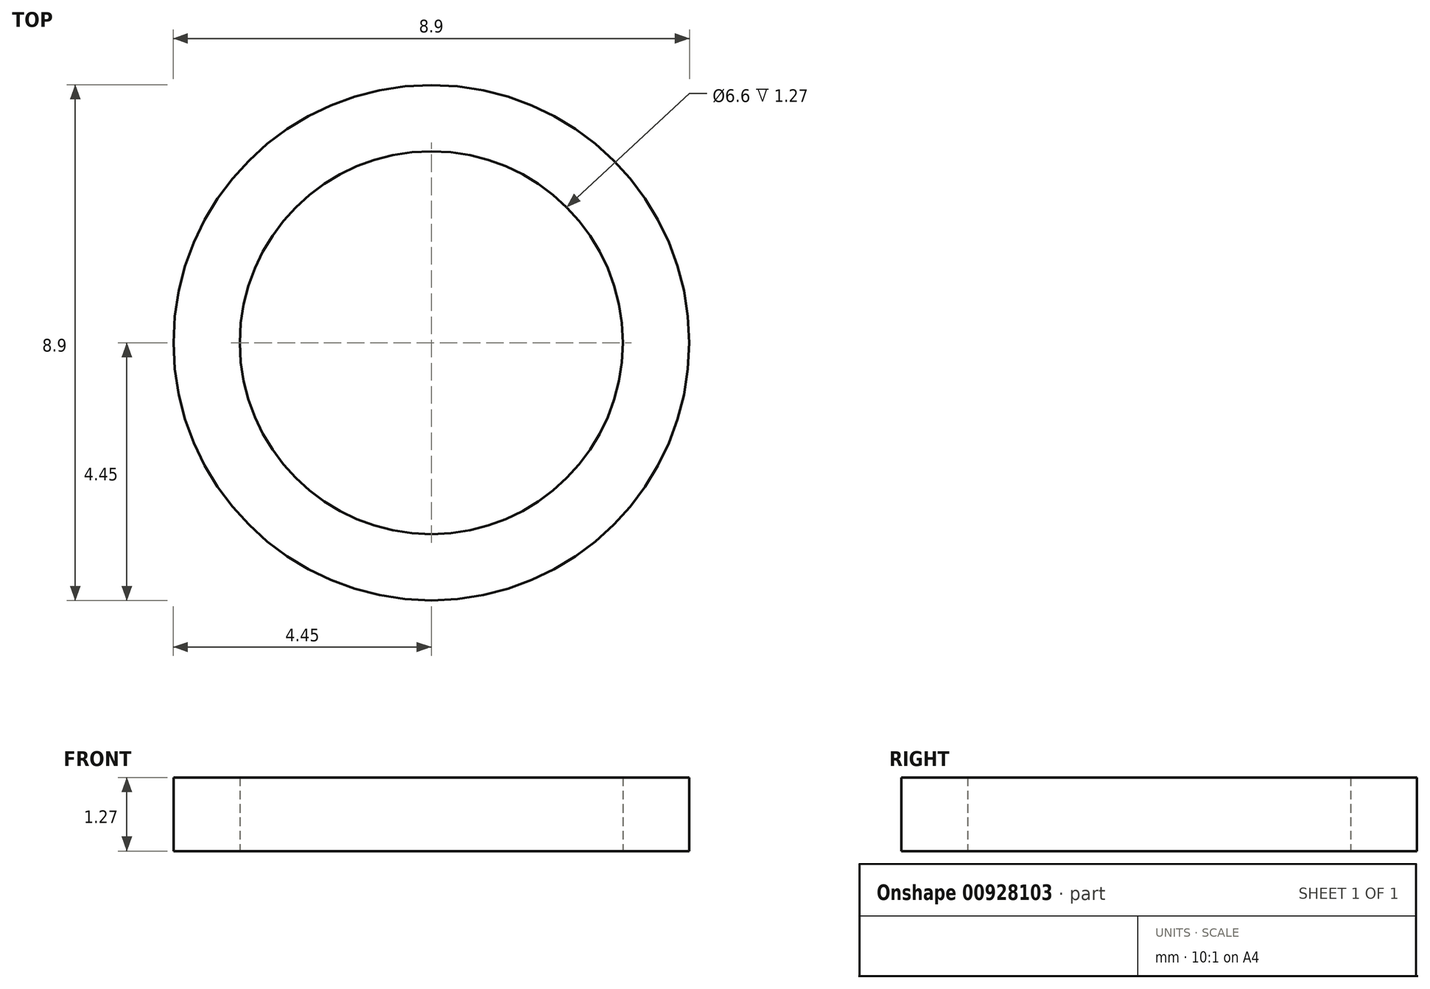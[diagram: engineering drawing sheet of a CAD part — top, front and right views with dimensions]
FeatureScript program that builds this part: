
annotation { "Feature Type Name" : "Feature", "Feature Type Description" : "" }
export const myFeature = defineFeature(function(context is Context, id is Id, definition is map)
    precondition{}
    {
        {
            var Q0;
            Q0=qCreatedBy(makeId("Top.planeOp"),FACE);
            var sketch = newSketch(context, id + "F0", { "sketchPlane" : qUnion([Q0])});
            skCircle(sketch, "E0", {"center": v(0, 0) * mm, "radius": 4.45 * mm});
            skCircle(sketch, "E1", {"center": v(0, 0) * mm, "radius": 3.3 * mm});
            skSolve(sketch);
        }
        {
            var Q0;
            Q0 = qSketchRegion(id + "F0", true);
            extrude(context, id + "F1", {"entities" : qUnion([Q0]), "depth" : 1.27 * mm, "offsetDistance" : 25.4 * mm});
        }
    });
